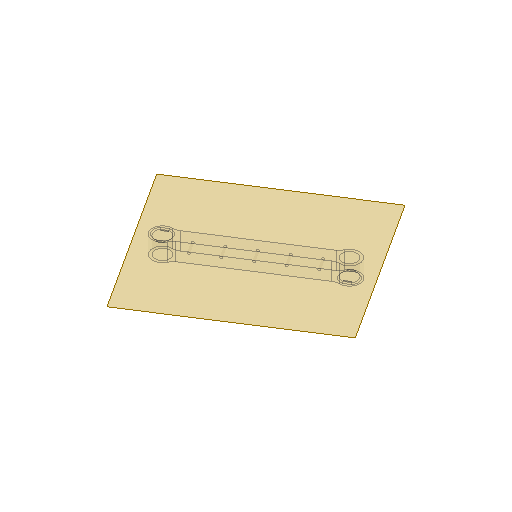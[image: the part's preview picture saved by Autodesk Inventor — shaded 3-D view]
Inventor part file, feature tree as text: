
AUTODESK INVENTOR PART (.ipt)
format: ipt  version: 2024.2 (Build 282272000, 272)  size: 138,240 bytes
history: native  units: in
note: dims shown in document units (in); Inventor stores cm internally (conversion verified against a paired STEP export)
features: other x4, plane x2
ambient origin geometry x8: Origin, YZ Plane, XZ Plane, XY Plane, X Axis, Y Axis, Z Axis, Center Point
bodies: Body1 (feature_tree)
feature tree (6):
  other  "5 Barras Version 0.ipt"
  plane  "Work Plane1"
  plane  "Work Plane2"
  other  "Distal Link 2::5 Barras Version 0.ipt"
  other  "TaggingFeature1"
  other  "Distal Link 2"
